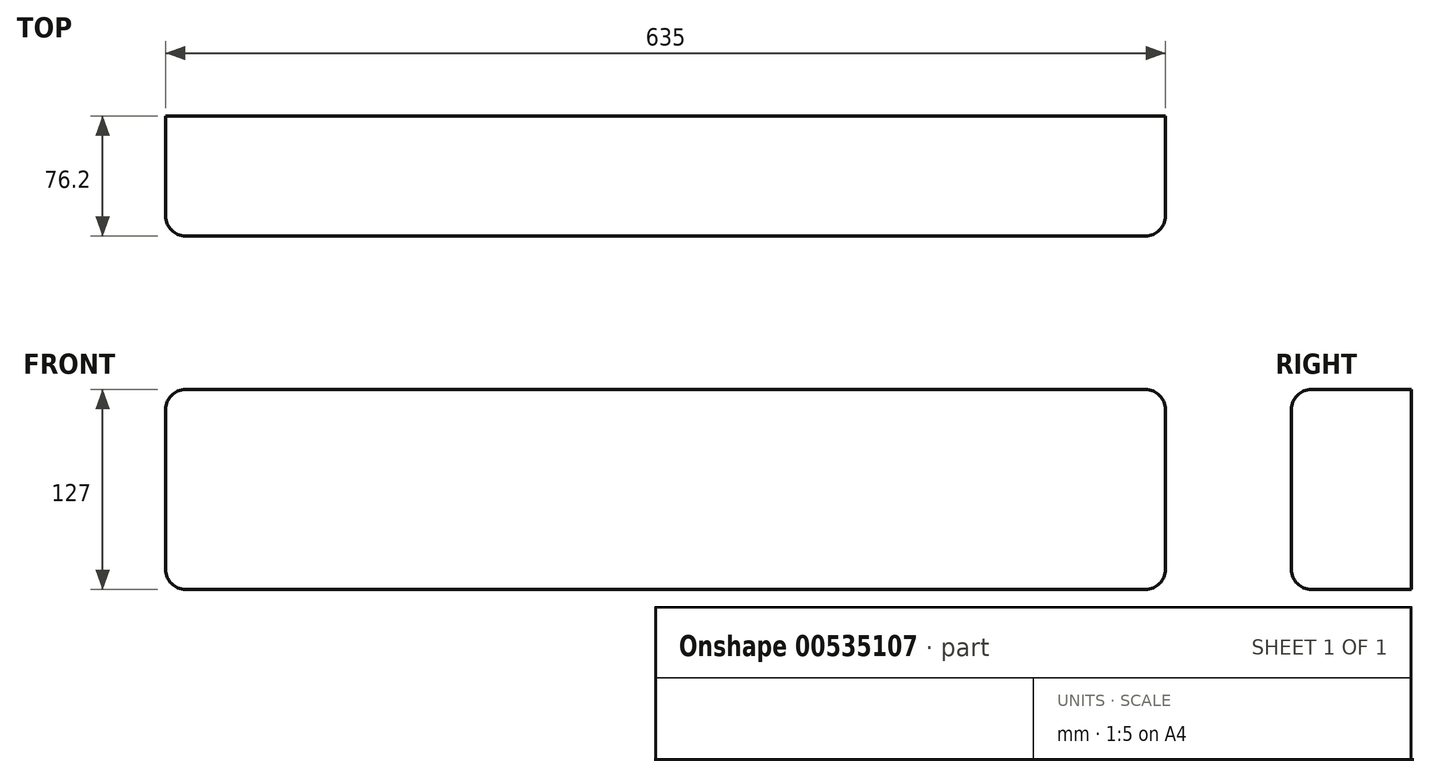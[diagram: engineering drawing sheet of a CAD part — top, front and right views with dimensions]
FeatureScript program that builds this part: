
annotation { "Feature Type Name" : "Feature", "Feature Type Description" : "" }
export const myFeature = defineFeature(function(context is Context, id is Id, definition is map)
    precondition{}
    {
        {
            var Q0;
            Q0=qCreatedBy(makeId("Front.planeOp"),FACE);
            var sketch = newSketch(context, id + "F0", { "sketchPlane" : qUnion([Q0])});
            skLineSegment(sketch, "E0.bottom", {"start": v(0, 0) * mm, "end": v(635, 0) * mm});
            skLineSegment(sketch, "E0.top", {"start": v(0, -127) * mm, "end": v(635, -127) * mm});
            skLineSegment(sketch, "E0.left", {"start": v(0, 0) * mm, "end": v(0, -127) * mm});
            skLineSegment(sketch, "E0.right", {"start": v(635, 0) * mm, "end": v(635, -127) * mm});
            skSolve(sketch);
        }
        {
            var Q0;
            Q0=makeQuery(id+"F0.imprint","IMPRINT",FACE,{"disambiguationData":[TD([[makeQuery(id+"F0.imprint","IMPRINT",EDGE,{"derivedFrom":sQuery(id+"F0.wireOp",EDGE,"E0.bottom")}),-1.0]])]});
            extrude(context, id + "F1", {"entities" : qUnion([Q0]), "depth" : 76.2 * mm});
        }
        {
            var Q0;
            Q0=makeQuery(id+"F1.opExtrude","CAP_EDGE",EDGE,{"disambiguationData":[OSD([sQuery(id+"F0.wireOp",EDGE,"E0.bottom")])],"isStart":false});
            var Q1;
            Q1=makeQuery(id+"F1.opExtrude","CAP_EDGE",EDGE,{"disambiguationData":[OSD([sQuery(id+"F0.wireOp",EDGE,"E0.left")])],"isStart":false});
            var Q2;
            Q2=makeQuery(id+"F1.opExtrude","CAP_EDGE",EDGE,{"disambiguationData":[OSD([sQuery(id+"F0.wireOp",EDGE,"E0.top")])],"isStart":false});
            var Q3;
            Q3=makeQuery(id+"F1.opExtrude","CAP_EDGE",EDGE,{"disambiguationData":[OSD([sQuery(id+"F0.wireOp",EDGE,"E0.right")])],"isStart":false});
            var Q4;
            Q4=makeQuery(id+"F1.opExtrude","SWEPT_EDGE",EDGE,{"disambiguationData":[OSD([sQuery(id+"F0.wireOp",EDGE,"E0.top"),sQuery(id+"F0.wireOp",EDGE,"E0.right")])]});
            var Q5;
            Q5=makeQuery(id+"F1.opExtrude","SWEPT_EDGE",EDGE,{"disambiguationData":[OSD([sQuery(id+"F0.wireOp",EDGE,"E0.bottom"),sQuery(id+"F0.wireOp",EDGE,"E0.right")])]});
            var Q6;
            Q6=makeQuery(id+"F1.opExtrude","SWEPT_EDGE",EDGE,{"disambiguationData":[OSD([sQuery(id+"F0.wireOp",EDGE,"E0.bottom"),sQuery(id+"F0.wireOp",EDGE,"E0.left")])]});
            var Q7;
            Q7=makeQuery(id+"F1.opExtrude","SWEPT_EDGE",EDGE,{"disambiguationData":[OSD([sQuery(id+"F0.wireOp",EDGE,"E0.top"),sQuery(id+"F0.wireOp",EDGE,"E0.left")])]});
            fillet(context, id + "F2", {"entities" : qUnion([Q0, Q1, Q2, Q3, Q4, Q5, Q6, Q7]), "radius" : 12.7 * mm, "tangentPropagation" : true, "allowEdgeOverflow" : false});
        }
    });
